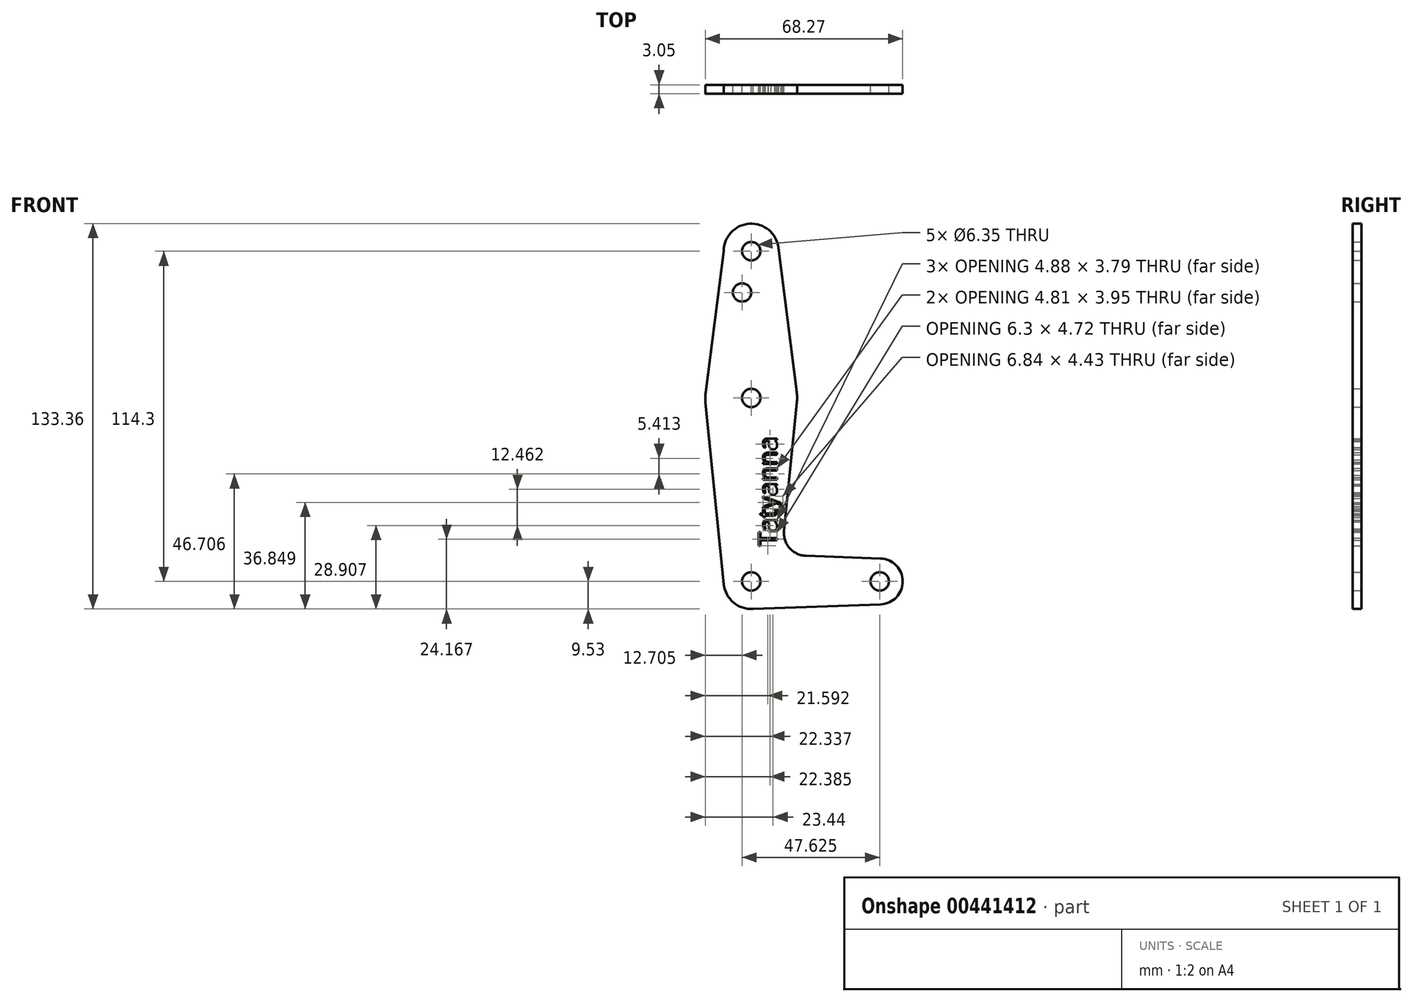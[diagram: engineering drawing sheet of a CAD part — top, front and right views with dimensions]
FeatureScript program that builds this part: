
annotation { "Feature Type Name" : "Feature", "Feature Type Description" : "" }
export const myFeature = defineFeature(function(context is Context, id is Id, definition is map)
    precondition{}
    {
        {
            var Q0;
            Q0=qCreatedBy(makeId("Front.planeOp"),FACE);
            var sketch = newSketch(context, id + "F0", { "sketchPlane" : qUnion([Q0])});
            skCircle(sketch, "E0", {"center": v(0, 0) * mm, "radius": 9.53 * mm});
            skLineSegment(sketch, "E1", {"start": v(0, 0) * mm, "end": v(0, 114.3) * mm, "construction": true});
            skLineSegment(sketch, "E2", {"start": v(0, 0) * mm, "end": v(44.45, 0) * mm, "construction": true});
            skCircle(sketch, "E3", {"center": v(44.45, 0) * mm, "radius": 7.94 * mm});
            skCircle(sketch, "E4", {"center": v(0, 114.3) * mm, "radius": 9.53 * mm});
            skCircle(sketch, "E5", {"center": v(0, 63.5) * mm, "radius": 15.88 * mm});
            skLineSegment(sketch, "E6", {"start": v(-9.53, 114.3) * mm, "end": v(-15.75, 65.5) * mm});
            skLineSegment(sketch, "E7", {"start": v(9.45, 115.5) * mm, "end": v(15.75, 65.48) * mm});
            skCircle(sketch, "E8", {"center": v(0, 114.3) * mm, "radius": 3.18 * mm});
            skCircle(sketch, "E9", {"center": v(0, 0) * mm, "radius": 3.18 * mm});
            skCircle(sketch, "E10", {"center": v(44.45, 0) * mm, "radius": 3.18 * mm});
            skCircle(sketch, "E11", {"center": v(0, 63.5) * mm, "radius": 3.18 * mm});
            skCircle(sketch, "E12", {"center": v(-3.18, 100.03) * mm, "radius": 3.18 * mm});
            skLineSegment(sketch, "E13", {"start": v(-15.8, 61.91) * mm, "end": v(-9.48, -0.95) * mm});
            skLineSegment(sketch, "E14", {"start": v(0, -9.53) * mm, "end": v(44.73, -7.93) * mm});
            skText(sketch, "E15", { "text": "Tatyanna", "fontName": "OpenSans-Regular.ttf"});
            skLineSegment(sketch, "E16", {"start": v(11.34, 17.6) * mm, "end": v(15.8, 61.91) * mm});
            skLineSegment(sketch, "E17", {"start": v(18.97, 8.85) * mm, "end": v(44.73, 7.93) * mm});
            skArc(sketch, "E18.filletArc", {"start": v(11.34, 17.6) * mm, "mid": v(13.26, 11.57) * mm, "end": v(18.97, 8.85) * mm});
            const initialGuessF0  = {"E15": [0.00886, 0.0122, 0, 1, 0.00635]};
            skSetInitialGuess(sketch, initialGuessF0);
            skSolve(sketch);
        }
        {
            var Q0;
            Q0 = qSketchRegion(id + "F0", true);
            extrude(context, id + "F1", {"entities" : qUnion([Q0]), "depth" : 3.05 * mm});
        }
    });
